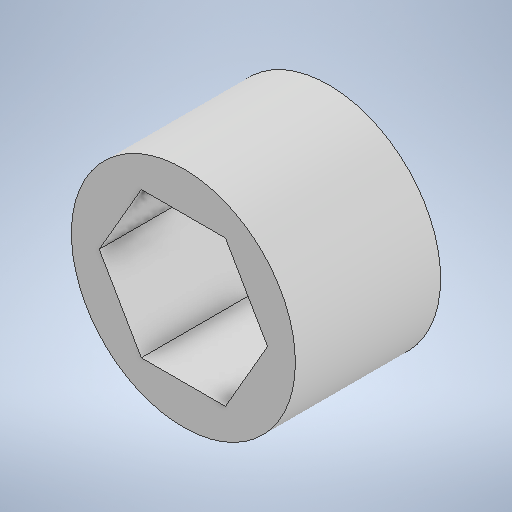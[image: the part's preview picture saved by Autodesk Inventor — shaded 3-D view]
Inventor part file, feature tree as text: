
AUTODESK INVENTOR PART (.ipt)
format: ipt  version: 2025.1 (Build 291241020, 241B)  size: 221,696 bytes
history: native  units: in
note: dims shown in document units (in); Inventor stores cm internally (conversion verified against a paired STEP export)
features: extrude x1, sketch x1
ambient origin geometry x8: Origin, YZ Plane, XZ Plane, XY Plane, X Axis, Y Axis, Z Axis, Center Point
bodies: Solid1 (feature_tree)
feature tree (2):
  extrude  "Extrusion1"  Depth=0.5in
  sketch  "Sketch1"  dims[d1=0.768in d2=0.5in d3=0.498in d4=0.0in]
